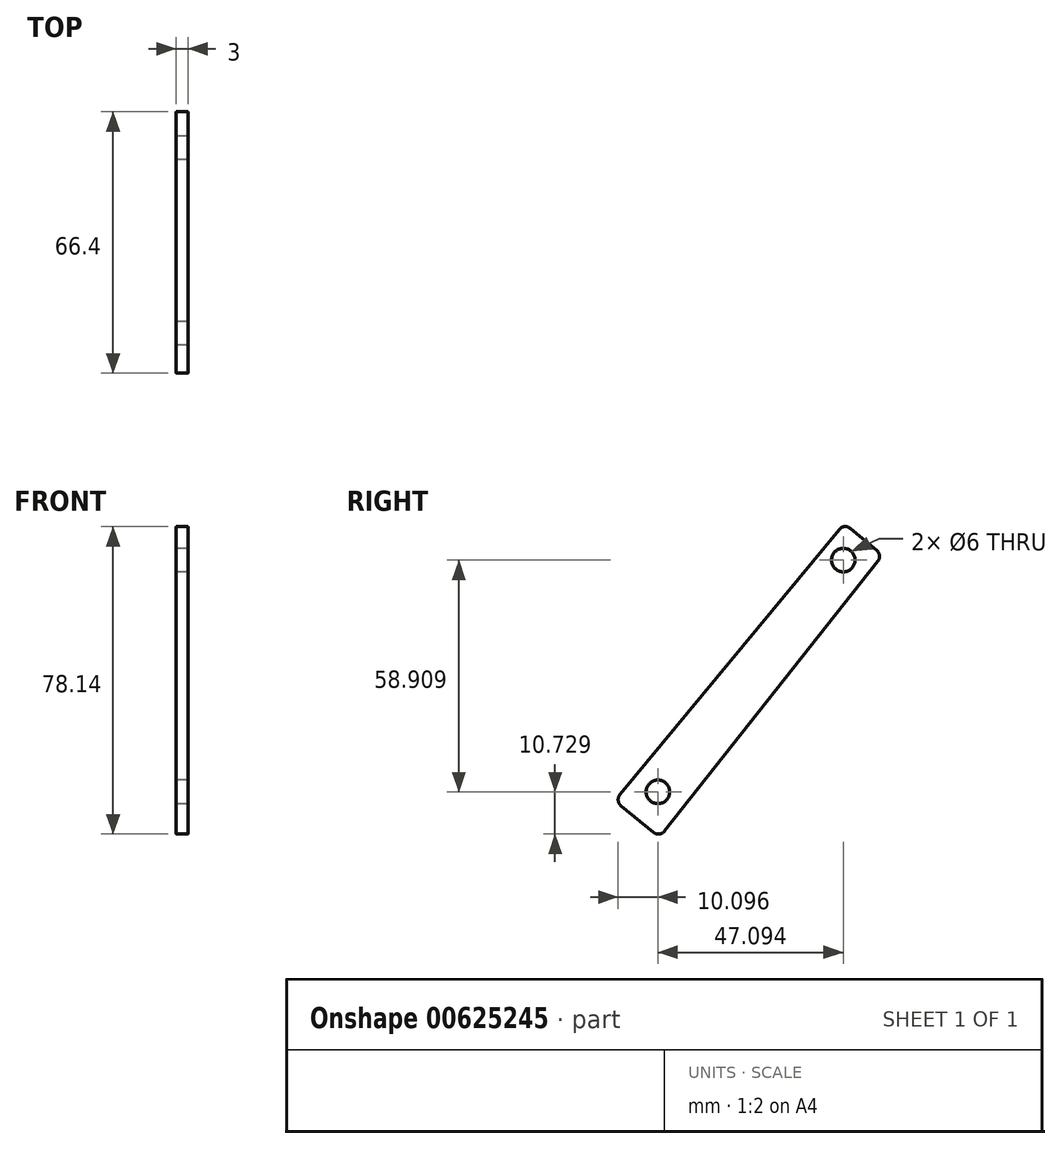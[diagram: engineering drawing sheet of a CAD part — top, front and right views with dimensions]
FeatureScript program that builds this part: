
annotation { "Feature Type Name" : "Feature", "Feature Type Description" : "" }
export const myFeature = defineFeature(function(context is Context, id is Id, definition is map)
    precondition{}
    {
        {
            var Q0;
            Q0=qCreatedBy(makeId("Right.planeOp"),FACE);
            var sketch = newSketch(context, id + "F0", { "sketchPlane" : qUnion([Q0])});
            skLineSegment(sketch, "E0", {"start": v(-37.9, -24.02) * mm, "end": v(17.8, 43.36) * mm});
            skLineSegment(sketch, "E1", {"start": v(20.61, 43.63) * mm, "end": v(27.33, 38.08) * mm});
            skLineSegment(sketch, "E2", {"start": v(27.62, 35.3) * mm, "end": v(-26.55, -33.29) * mm});
            skLineSegment(sketch, "E3", {"start": v(-29.4, -33.6) * mm, "end": v(-37.62, -26.84) * mm});
            skCircle(sketch, "E4", {"center": v(18.84, 35.59) * mm, "radius": 3 * mm});
            skCircle(sketch, "E5", {"center": v(-28.25, -23.32) * mm, "radius": 3 * mm});
            skLineSegment(sketch, "E6", {"start": v(18.84, 35.59) * mm, "end": v(18.84, 38.59) * mm, "construction": true});
            skPoint(sketch, "E7.visualSharp", {"position": v(19.07, 44.9) * mm});
            skArc(sketch, "E7.filletArc", {"start": v(20.61, 43.63) * mm, "mid": v(19.15, 44.08) * mm, "end": v(17.8, 43.36) * mm});
            skPoint(sketch, "E8.visualSharp", {"position": v(28.84, 36.83) * mm});
            skArc(sketch, "E8.filletArc", {"start": v(27.62, 35.3) * mm, "mid": v(28.04, 36.75) * mm, "end": v(27.33, 38.08) * mm});
            skPoint(sketch, "E9.visualSharp", {"position": v(-27.82, -34.89) * mm});
            skArc(sketch, "E9.filletArc", {"start": v(-29.4, -33.6) * mm, "mid": v(-27.9, -34.04) * mm, "end": v(-26.55, -33.29) * mm});
            skPoint(sketch, "E10.visualSharp", {"position": v(-39.17, -25.57) * mm});
            skArc(sketch, "E10.filletArc", {"start": v(-37.9, -24.02) * mm, "mid": v(-38.35, -25.49) * mm, "end": v(-37.62, -26.84) * mm});
            skSolve(sketch);
        }
        {
            var Q0;
            Q0=makeQuery(id+"F0.imprint","IMPRINT",FACE,{"disambiguationData":[TD([[makeQuery(id+"F0.imprint","IMPRINT",EDGE,{"derivedFrom":sQuery(id+"F0.wireOp",EDGE,"E0")}),-1.0]])]});
            extrude(context, id + "F1", {"entities" : qUnion([Q0]), "depth" : 3 * mm, "offsetDistance" : 25 * mm});
        }
    });
